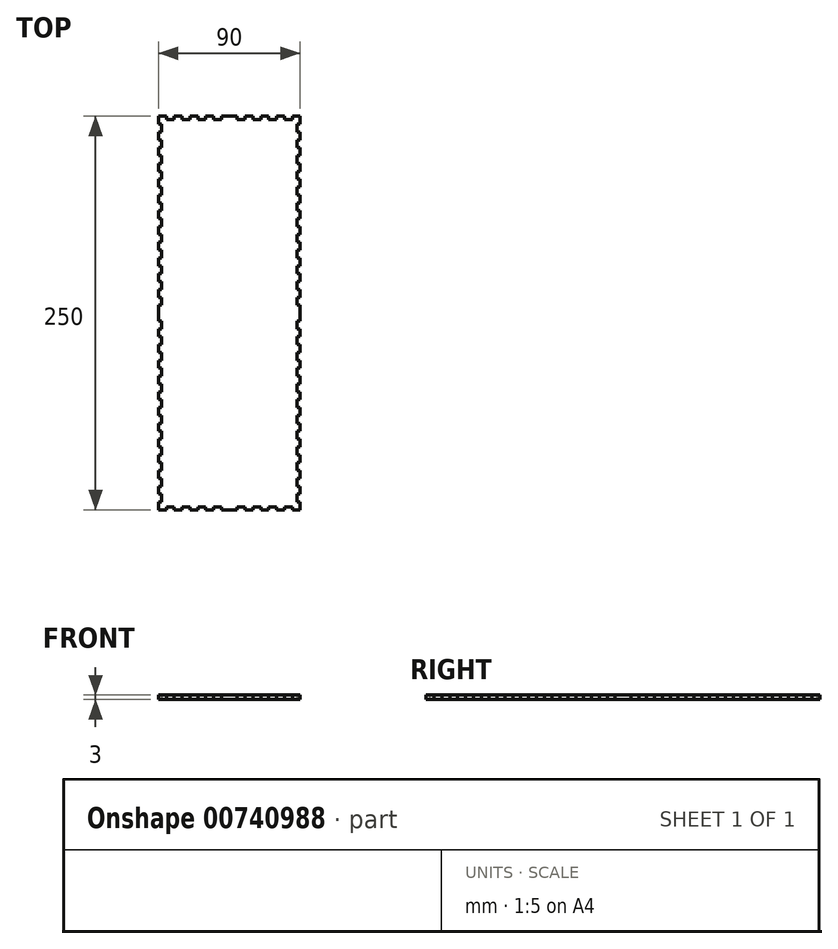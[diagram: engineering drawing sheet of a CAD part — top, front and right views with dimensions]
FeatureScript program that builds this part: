
annotation { "Feature Type Name" : "Feature", "Feature Type Description" : "" }
export const myFeature = defineFeature(function(context is Context, id is Id, definition is map)
    precondition{}
    {
        {
            var Q0;
            Q0=qCreatedBy(makeId("Top.planeOp"),FACE);
            var sketch = newSketch(context, id + "F0", { "sketchPlane" : qUnion([Q0])});
            skLineSegment(sketch, "E0.bottom", {"start": v(-45, 125) * mm, "end": v(-40, 125) * mm});
            skLineSegment(sketch, "E0.top", {"start": v(-45, -125) * mm, "end": v(-40, -125) * mm});
            skLineSegment(sketch, "E0.left", {"start": v(-45, 125) * mm, "end": v(-45, 120) * mm});
            skLineSegment(sketch, "E0.right", {"start": v(45, 125) * mm, "end": v(45, 120) * mm});
            skPoint(sketch, "E1", {"position": v(0, 0) * mm});
            skLineSegment(sketch, "E2", {"start": v(-45, 125) * mm, "end": v(45, -125) * mm, "construction": true});
            skLineSegment(sketch, "E3", {"start": v(45, 125) * mm, "end": v(-45, -125) * mm, "construction": true});
            skLineSegment(sketch, "E4.top", {"start": v(-40, 123) * mm, "end": v(-35, 123) * mm});
            skLineSegment(sketch, "E4.left", {"start": v(-40, 125) * mm, "end": v(-40, 123) * mm});
            skLineSegment(sketch, "E4.right", {"start": v(-35, 125) * mm, "end": v(-35, 123) * mm});
            skLineSegment(sketch, "E5.top", {"start": v(-30, 123) * mm, "end": v(-25, 123) * mm});
            skLineSegment(sketch, "E5.left", {"start": v(-30, 125) * mm, "end": v(-30, 123) * mm});
            skLineSegment(sketch, "E5.right", {"start": v(-25, 125) * mm, "end": v(-25, 123) * mm});
            skLineSegment(sketch, "E6", {"start": v(-45, 0) * mm, "end": v(45, 0) * mm, "construction": true});
            skLineSegment(sketch, "E7.top", {"start": v(-20, 123) * mm, "end": v(-15, 123) * mm});
            skLineSegment(sketch, "E7.left", {"start": v(-20, 125) * mm, "end": v(-20, 123) * mm});
            skLineSegment(sketch, "E7.right", {"start": v(-15, 125) * mm, "end": v(-15, 123) * mm});
            skLineSegment(sketch, "E8.top", {"start": v(-10, 123) * mm, "end": v(-5, 123) * mm});
            skLineSegment(sketch, "E8.left", {"start": v(-10, 125) * mm, "end": v(-10, 123) * mm});
            skLineSegment(sketch, "E8.right", {"start": v(-5, 125) * mm, "end": v(-5, 123) * mm});
            skLineSegment(sketch, "E9.top", {"start": v(5, 123) * mm, "end": v(10, 123) * mm});
            skLineSegment(sketch, "E9.left", {"start": v(5, 125) * mm, "end": v(5, 123) * mm});
            skLineSegment(sketch, "E9.right", {"start": v(10, 125) * mm, "end": v(10, 123) * mm});
            skLineSegment(sketch, "E10.top", {"start": v(15, 123) * mm, "end": v(20, 123) * mm});
            skLineSegment(sketch, "E10.left", {"start": v(15, 125) * mm, "end": v(15, 123) * mm});
            skLineSegment(sketch, "E10.right", {"start": v(20, 125) * mm, "end": v(20, 123) * mm});
            skLineSegment(sketch, "E11.top", {"start": v(25, 123) * mm, "end": v(30, 123) * mm});
            skLineSegment(sketch, "E11.left", {"start": v(25, 125) * mm, "end": v(25, 123) * mm});
            skLineSegment(sketch, "E11.right", {"start": v(30, 125) * mm, "end": v(30, 123) * mm});
            skLineSegment(sketch, "E12.top", {"start": v(35, 123) * mm, "end": v(40, 123) * mm});
            skLineSegment(sketch, "E12.left", {"start": v(35, 125) * mm, "end": v(35, 123) * mm});
            skLineSegment(sketch, "E12.right", {"start": v(40, 125) * mm, "end": v(40, 123) * mm});
            skLineSegment(sketch, "E13.bottom", {"start": v(-40, -123) * mm, "end": v(-35, -123) * mm});
            skLineSegment(sketch, "E13.left", {"start": v(-40, -123) * mm, "end": v(-40, -125) * mm});
            skLineSegment(sketch, "E13.right", {"start": v(-35, -123) * mm, "end": v(-35, -125) * mm});
            skLineSegment(sketch, "E14.bottom", {"start": v(-30, -123) * mm, "end": v(-25, -123) * mm});
            skLineSegment(sketch, "E14.left", {"start": v(-30, -123) * mm, "end": v(-30, -125) * mm});
            skLineSegment(sketch, "E14.right", {"start": v(-25, -123) * mm, "end": v(-25, -125) * mm});
            skLineSegment(sketch, "E15.bottom", {"start": v(-20, -123) * mm, "end": v(-15, -123) * mm});
            skLineSegment(sketch, "E15.left", {"start": v(-20, -123) * mm, "end": v(-20, -125) * mm});
            skLineSegment(sketch, "E15.right", {"start": v(-15, -123) * mm, "end": v(-15, -125) * mm});
            skLineSegment(sketch, "E16.bottom", {"start": v(-10, -123) * mm, "end": v(-5, -123) * mm});
            skLineSegment(sketch, "E16.left", {"start": v(-10, -123) * mm, "end": v(-10, -125) * mm});
            skLineSegment(sketch, "E16.right", {"start": v(-5, -123) * mm, "end": v(-5, -125) * mm});
            skLineSegment(sketch, "E17.bottom", {"start": v(5, -123) * mm, "end": v(10, -123) * mm});
            skLineSegment(sketch, "E17.left", {"start": v(5, -123) * mm, "end": v(5, -125) * mm});
            skLineSegment(sketch, "E17.right", {"start": v(10, -123) * mm, "end": v(10, -125) * mm});
            skLineSegment(sketch, "E18.bottom", {"start": v(15, -123) * mm, "end": v(20, -123) * mm});
            skLineSegment(sketch, "E18.left", {"start": v(15, -123) * mm, "end": v(15, -125) * mm});
            skLineSegment(sketch, "E18.right", {"start": v(20, -123) * mm, "end": v(20, -125) * mm});
            skLineSegment(sketch, "E19.bottom", {"start": v(25, -123) * mm, "end": v(30, -123) * mm});
            skLineSegment(sketch, "E19.left", {"start": v(25, -123) * mm, "end": v(25, -125) * mm});
            skLineSegment(sketch, "E19.right", {"start": v(30, -123) * mm, "end": v(30, -125) * mm});
            skLineSegment(sketch, "E20.bottom", {"start": v(35, -123) * mm, "end": v(40, -123) * mm});
            skLineSegment(sketch, "E20.left", {"start": v(35, -123) * mm, "end": v(35, -125) * mm});
            skLineSegment(sketch, "E20.right", {"start": v(40, -123) * mm, "end": v(40, -125) * mm});
            skLineSegment(sketch, "E21.bottom", {"start": v(43, 45) * mm, "end": v(43, 50) * mm});
            skLineSegment(sketch, "E21.left", {"start": v(43, 45) * mm, "end": v(45, 45) * mm});
            skLineSegment(sketch, "E21.right", {"start": v(43, 50) * mm, "end": v(45, 50) * mm});
            skLineSegment(sketch, "E22.bottom", {"start": v(43, 55) * mm, "end": v(43, 60) * mm});
            skLineSegment(sketch, "E22.left", {"start": v(43, 55) * mm, "end": v(45, 55) * mm});
            skLineSegment(sketch, "E22.right", {"start": v(43, 60) * mm, "end": v(45, 60) * mm});
            skLineSegment(sketch, "E23.bottom", {"start": v(43, 65) * mm, "end": v(43, 70) * mm});
            skLineSegment(sketch, "E23.left", {"start": v(43, 65) * mm, "end": v(45, 65) * mm});
            skLineSegment(sketch, "E23.right", {"start": v(43, 70) * mm, "end": v(45, 70) * mm});
            skLineSegment(sketch, "E24.bottom", {"start": v(43, 75) * mm, "end": v(43, 80) * mm});
            skLineSegment(sketch, "E24.left", {"start": v(43, 75) * mm, "end": v(45, 75) * mm});
            skLineSegment(sketch, "E24.right", {"start": v(43, 80) * mm, "end": v(45, 80) * mm});
            skLineSegment(sketch, "E25.bottom", {"start": v(43, 85) * mm, "end": v(43, 90) * mm});
            skLineSegment(sketch, "E25.left", {"start": v(43, 85) * mm, "end": v(45, 85) * mm});
            skLineSegment(sketch, "E25.right", {"start": v(43, 90) * mm, "end": v(45, 90) * mm});
            skLineSegment(sketch, "E26.bottom", {"start": v(43, 95) * mm, "end": v(43, 100) * mm});
            skLineSegment(sketch, "E26.left", {"start": v(43, 95) * mm, "end": v(45, 95) * mm});
            skLineSegment(sketch, "E26.right", {"start": v(43, 100) * mm, "end": v(45, 100) * mm});
            skLineSegment(sketch, "E27.bottom", {"start": v(43, 105) * mm, "end": v(43, 110) * mm});
            skLineSegment(sketch, "E27.left", {"start": v(43, 105) * mm, "end": v(45, 105) * mm});
            skLineSegment(sketch, "E27.right", {"start": v(43, 110) * mm, "end": v(45, 110) * mm});
            skLineSegment(sketch, "E28.bottom", {"start": v(43, 115) * mm, "end": v(43, 120) * mm});
            skLineSegment(sketch, "E28.left", {"start": v(43, 115) * mm, "end": v(45, 115) * mm});
            skLineSegment(sketch, "E28.right", {"start": v(43, 120) * mm, "end": v(45, 120) * mm});
            skLineSegment(sketch, "E29.bottom", {"start": v(43, 15) * mm, "end": v(43, 20) * mm});
            skLineSegment(sketch, "E29.left", {"start": v(43, 15) * mm, "end": v(45, 15) * mm});
            skLineSegment(sketch, "E29.right", {"start": v(43, 20) * mm, "end": v(45, 20) * mm});
            skLineSegment(sketch, "E30.bottom", {"start": v(43, 25) * mm, "end": v(43, 30) * mm});
            skLineSegment(sketch, "E30.left", {"start": v(43, 25) * mm, "end": v(45, 25) * mm});
            skLineSegment(sketch, "E30.right", {"start": v(43, 30) * mm, "end": v(45, 30) * mm});
            skLineSegment(sketch, "E31.bottom", {"start": v(43, 35) * mm, "end": v(43, 40) * mm});
            skLineSegment(sketch, "E31.left", {"start": v(43, 35) * mm, "end": v(45, 35) * mm});
            skLineSegment(sketch, "E31.right", {"start": v(43, 40) * mm, "end": v(45, 40) * mm});
            skLineSegment(sketch, "E32.bottom", {"start": v(43, -90) * mm, "end": v(43, -85) * mm});
            skLineSegment(sketch, "E32.left", {"start": v(43, -90) * mm, "end": v(45, -90) * mm});
            skLineSegment(sketch, "E32.right", {"start": v(43, -85) * mm, "end": v(45, -85) * mm});
            skLineSegment(sketch, "E33.bottom", {"start": v(43, -80) * mm, "end": v(43, -75) * mm});
            skLineSegment(sketch, "E33.left", {"start": v(43, -80) * mm, "end": v(45, -80) * mm});
            skLineSegment(sketch, "E33.right", {"start": v(43, -75) * mm, "end": v(45, -75) * mm});
            skLineSegment(sketch, "E34.bottom", {"start": v(43, -70) * mm, "end": v(43, -65) * mm});
            skLineSegment(sketch, "E34.left", {"start": v(43, -70) * mm, "end": v(45, -70) * mm});
            skLineSegment(sketch, "E34.right", {"start": v(43, -65) * mm, "end": v(45, -65) * mm});
            skLineSegment(sketch, "E35.bottom", {"start": v(43, -60) * mm, "end": v(43, -55) * mm});
            skLineSegment(sketch, "E35.left", {"start": v(43, -60) * mm, "end": v(45, -60) * mm});
            skLineSegment(sketch, "E35.right", {"start": v(43, -55) * mm, "end": v(45, -55) * mm});
            skLineSegment(sketch, "E36.bottom", {"start": v(43, -50) * mm, "end": v(43, -45) * mm});
            skLineSegment(sketch, "E36.left", {"start": v(43, -50) * mm, "end": v(45, -50) * mm});
            skLineSegment(sketch, "E36.right", {"start": v(43, -45) * mm, "end": v(45, -45) * mm});
            skLineSegment(sketch, "E37.bottom", {"start": v(43, -40) * mm, "end": v(43, -35) * mm});
            skLineSegment(sketch, "E37.left", {"start": v(43, -40) * mm, "end": v(45, -40) * mm});
            skLineSegment(sketch, "E37.right", {"start": v(43, -35) * mm, "end": v(45, -35) * mm});
            skLineSegment(sketch, "E38.bottom", {"start": v(43, -30) * mm, "end": v(43, -25) * mm});
            skLineSegment(sketch, "E38.left", {"start": v(43, -30) * mm, "end": v(45, -30) * mm});
            skLineSegment(sketch, "E38.right", {"start": v(43, -25) * mm, "end": v(45, -25) * mm});
            skLineSegment(sketch, "E39.bottom", {"start": v(43, -20) * mm, "end": v(43, -15) * mm});
            skLineSegment(sketch, "E39.left", {"start": v(43, -20) * mm, "end": v(45, -20) * mm});
            skLineSegment(sketch, "E39.right", {"start": v(43, -15) * mm, "end": v(45, -15) * mm});
            skLineSegment(sketch, "E40.bottom", {"start": v(43, -120) * mm, "end": v(43, -115) * mm});
            skLineSegment(sketch, "E40.left", {"start": v(43, -120) * mm, "end": v(45, -120) * mm});
            skLineSegment(sketch, "E40.right", {"start": v(43, -115) * mm, "end": v(45, -115) * mm});
            skLineSegment(sketch, "E41.bottom", {"start": v(43, -110) * mm, "end": v(43, -105) * mm});
            skLineSegment(sketch, "E41.left", {"start": v(43, -110) * mm, "end": v(45, -110) * mm});
            skLineSegment(sketch, "E41.right", {"start": v(43, -105) * mm, "end": v(45, -105) * mm});
            skLineSegment(sketch, "E42.bottom", {"start": v(43, -100) * mm, "end": v(43, -95) * mm});
            skLineSegment(sketch, "E42.left", {"start": v(43, -100) * mm, "end": v(45, -100) * mm});
            skLineSegment(sketch, "E42.right", {"start": v(43, -95) * mm, "end": v(45, -95) * mm});
            skLineSegment(sketch, "E43.top", {"start": v(-43, 45) * mm, "end": v(-43, 50) * mm});
            skLineSegment(sketch, "E43.left", {"start": v(-45, 45) * mm, "end": v(-43, 45) * mm});
            skLineSegment(sketch, "E43.right", {"start": v(-45, 50) * mm, "end": v(-43, 50) * mm});
            skLineSegment(sketch, "E44.top", {"start": v(-43, 55) * mm, "end": v(-43, 60) * mm});
            skLineSegment(sketch, "E44.left", {"start": v(-45, 55) * mm, "end": v(-43, 55) * mm});
            skLineSegment(sketch, "E44.right", {"start": v(-45, 60) * mm, "end": v(-43, 60) * mm});
            skLineSegment(sketch, "E45.top", {"start": v(-43, 65) * mm, "end": v(-43, 70) * mm});
            skLineSegment(sketch, "E45.left", {"start": v(-45, 65) * mm, "end": v(-43, 65) * mm});
            skLineSegment(sketch, "E45.right", {"start": v(-45, 70) * mm, "end": v(-43, 70) * mm});
            skLineSegment(sketch, "E46.top", {"start": v(-43, 75) * mm, "end": v(-43, 80) * mm});
            skLineSegment(sketch, "E46.left", {"start": v(-45, 75) * mm, "end": v(-43, 75) * mm});
            skLineSegment(sketch, "E46.right", {"start": v(-45, 80) * mm, "end": v(-43, 80) * mm});
            skLineSegment(sketch, "E47.top", {"start": v(-43, 85) * mm, "end": v(-43, 90) * mm});
            skLineSegment(sketch, "E47.left", {"start": v(-45, 85) * mm, "end": v(-43, 85) * mm});
            skLineSegment(sketch, "E47.right", {"start": v(-45, 90) * mm, "end": v(-43, 90) * mm});
            skLineSegment(sketch, "E48.top", {"start": v(-43, 95) * mm, "end": v(-43, 100) * mm});
            skLineSegment(sketch, "E48.left", {"start": v(-45, 95) * mm, "end": v(-43, 95) * mm});
            skLineSegment(sketch, "E48.right", {"start": v(-45, 100) * mm, "end": v(-43, 100) * mm});
            skLineSegment(sketch, "E49.top", {"start": v(-43, 105) * mm, "end": v(-43, 110) * mm});
            skLineSegment(sketch, "E49.left", {"start": v(-45, 105) * mm, "end": v(-43, 105) * mm});
            skLineSegment(sketch, "E49.right", {"start": v(-45, 110) * mm, "end": v(-43, 110) * mm});
            skLineSegment(sketch, "E50.top", {"start": v(-43, 115) * mm, "end": v(-43, 120) * mm});
            skLineSegment(sketch, "E50.left", {"start": v(-45, 115) * mm, "end": v(-43, 115) * mm});
            skLineSegment(sketch, "E50.right", {"start": v(-45, 120) * mm, "end": v(-43, 120) * mm});
            skLineSegment(sketch, "E51.top", {"start": v(-43, 15) * mm, "end": v(-43, 20) * mm});
            skLineSegment(sketch, "E51.left", {"start": v(-45, 15) * mm, "end": v(-43, 15) * mm});
            skLineSegment(sketch, "E51.right", {"start": v(-45, 20) * mm, "end": v(-43, 20) * mm});
            skLineSegment(sketch, "E52.top", {"start": v(-43, 25) * mm, "end": v(-43, 30) * mm});
            skLineSegment(sketch, "E52.left", {"start": v(-45, 25) * mm, "end": v(-43, 25) * mm});
            skLineSegment(sketch, "E52.right", {"start": v(-45, 30) * mm, "end": v(-43, 30) * mm});
            skLineSegment(sketch, "E53.top", {"start": v(-43, 35) * mm, "end": v(-43, 40) * mm});
            skLineSegment(sketch, "E53.left", {"start": v(-45, 35) * mm, "end": v(-43, 35) * mm});
            skLineSegment(sketch, "E53.right", {"start": v(-45, 40) * mm, "end": v(-43, 40) * mm});
            skLineSegment(sketch, "E54.top", {"start": v(-43, -90) * mm, "end": v(-43, -85) * mm});
            skLineSegment(sketch, "E54.left", {"start": v(-45, -90) * mm, "end": v(-43, -90) * mm});
            skLineSegment(sketch, "E54.right", {"start": v(-45, -85) * mm, "end": v(-43, -85) * mm});
            skLineSegment(sketch, "E55.top", {"start": v(-43, -80) * mm, "end": v(-43, -75) * mm});
            skLineSegment(sketch, "E55.left", {"start": v(-45, -80) * mm, "end": v(-43, -80) * mm});
            skLineSegment(sketch, "E55.right", {"start": v(-45, -75) * mm, "end": v(-43, -75) * mm});
            skLineSegment(sketch, "E56.top", {"start": v(-43, -70) * mm, "end": v(-43, -65) * mm});
            skLineSegment(sketch, "E56.left", {"start": v(-45, -70) * mm, "end": v(-43, -70) * mm});
            skLineSegment(sketch, "E56.right", {"start": v(-45, -65) * mm, "end": v(-43, -65) * mm});
            skLineSegment(sketch, "E57.top", {"start": v(-43, -60) * mm, "end": v(-43, -55) * mm});
            skLineSegment(sketch, "E57.left", {"start": v(-45, -60) * mm, "end": v(-43, -60) * mm});
            skLineSegment(sketch, "E57.right", {"start": v(-45, -55) * mm, "end": v(-43, -55) * mm});
            skLineSegment(sketch, "E58.top", {"start": v(-43, -50) * mm, "end": v(-43, -45) * mm});
            skLineSegment(sketch, "E58.left", {"start": v(-45, -50) * mm, "end": v(-43, -50) * mm});
            skLineSegment(sketch, "E58.right", {"start": v(-45, -45) * mm, "end": v(-43, -45) * mm});
            skLineSegment(sketch, "E59.top", {"start": v(-43, -40) * mm, "end": v(-43, -35) * mm});
            skLineSegment(sketch, "E59.left", {"start": v(-45, -40) * mm, "end": v(-43, -40) * mm});
            skLineSegment(sketch, "E59.right", {"start": v(-45, -35) * mm, "end": v(-43, -35) * mm});
            skLineSegment(sketch, "E60.top", {"start": v(-43, -30) * mm, "end": v(-43, -25) * mm});
            skLineSegment(sketch, "E60.left", {"start": v(-45, -30) * mm, "end": v(-43, -30) * mm});
            skLineSegment(sketch, "E60.right", {"start": v(-45, -25) * mm, "end": v(-43, -25) * mm});
            skLineSegment(sketch, "E61.top", {"start": v(-43, -20) * mm, "end": v(-43, -15) * mm});
            skLineSegment(sketch, "E61.left", {"start": v(-45, -20) * mm, "end": v(-43, -20) * mm});
            skLineSegment(sketch, "E61.right", {"start": v(-45, -15) * mm, "end": v(-43, -15) * mm});
            skLineSegment(sketch, "E62.top", {"start": v(-43, -120) * mm, "end": v(-43, -115) * mm});
            skLineSegment(sketch, "E62.left", {"start": v(-45, -120) * mm, "end": v(-43, -120) * mm});
            skLineSegment(sketch, "E62.right", {"start": v(-45, -115) * mm, "end": v(-43, -115) * mm});
            skLineSegment(sketch, "E63.top", {"start": v(-43, -110) * mm, "end": v(-43, -105) * mm});
            skLineSegment(sketch, "E63.left", {"start": v(-45, -110) * mm, "end": v(-43, -110) * mm});
            skLineSegment(sketch, "E63.right", {"start": v(-45, -105) * mm, "end": v(-43, -105) * mm});
            skLineSegment(sketch, "E64.top", {"start": v(-43, -100) * mm, "end": v(-43, -95) * mm});
            skLineSegment(sketch, "E64.left", {"start": v(-45, -100) * mm, "end": v(-43, -100) * mm});
            skLineSegment(sketch, "E64.right", {"start": v(-45, -95) * mm, "end": v(-43, -95) * mm});
            skLineSegment(sketch, "E65.top", {"start": v(-43, 5) * mm, "end": v(-43, 10) * mm});
            skLineSegment(sketch, "E65.left", {"start": v(-45, 5) * mm, "end": v(-43, 5) * mm});
            skLineSegment(sketch, "E65.right", {"start": v(-45, 10) * mm, "end": v(-43, 10) * mm});
            skLineSegment(sketch, "E66.top", {"start": v(-43, -10) * mm, "end": v(-43, -5) * mm});
            skLineSegment(sketch, "E66.left", {"start": v(-45, -10) * mm, "end": v(-43, -10) * mm});
            skLineSegment(sketch, "E66.right", {"start": v(-45, -5) * mm, "end": v(-43, -5) * mm});
            skLineSegment(sketch, "E67.bottom", {"start": v(43, -10) * mm, "end": v(43, -5) * mm});
            skLineSegment(sketch, "E67.left", {"start": v(43, -10) * mm, "end": v(45, -10) * mm});
            skLineSegment(sketch, "E67.right", {"start": v(43, -5) * mm, "end": v(45, -5) * mm});
            skLineSegment(sketch, "E68.bottom", {"start": v(43, 5) * mm, "end": v(43, 10) * mm});
            skLineSegment(sketch, "E68.left", {"start": v(43, 5) * mm, "end": v(45, 5) * mm});
            skLineSegment(sketch, "E68.right", {"start": v(43, 10) * mm, "end": v(45, 10) * mm});
            skLineSegment(sketch, "E69.trimOffspring", {"start": v(-35, 125) * mm, "end": v(-30, 125) * mm});
            skLineSegment(sketch, "E70.trimOffspring", {"start": v(-25, 125) * mm, "end": v(-20, 125) * mm});
            skLineSegment(sketch, "E71.trimOffspring", {"start": v(-15, 125) * mm, "end": v(-10, 125) * mm});
            skLineSegment(sketch, "E72.trimOffspring", {"start": v(-5, 125) * mm, "end": v(5, 125) * mm});
            skLineSegment(sketch, "E73.trimOffspring", {"start": v(10, 125) * mm, "end": v(15, 125) * mm});
            skLineSegment(sketch, "E74.trimOffspring", {"start": v(20, 125) * mm, "end": v(25, 125) * mm});
            skLineSegment(sketch, "E75.trimOffspring", {"start": v(30, 125) * mm, "end": v(35, 125) * mm});
            skLineSegment(sketch, "E76.trimOffspring", {"start": v(40, 125) * mm, "end": v(45, 125) * mm});
            skLineSegment(sketch, "E77.trimOffspring", {"start": v(45, 115) * mm, "end": v(45, 110) * mm});
            skLineSegment(sketch, "E78.trimOffspring", {"start": v(45, 105) * mm, "end": v(45, 100) * mm});
            skLineSegment(sketch, "E79.trimOffspring", {"start": v(45, 95) * mm, "end": v(45, 90) * mm});
            skLineSegment(sketch, "E80.trimOffspring", {"start": v(45, 85) * mm, "end": v(45, 80) * mm});
            skLineSegment(sketch, "E81.trimOffspring", {"start": v(45, 75) * mm, "end": v(45, 70) * mm});
            skLineSegment(sketch, "E82.trimOffspring", {"start": v(45, 65) * mm, "end": v(45, 60) * mm});
            skLineSegment(sketch, "E83.trimOffspring", {"start": v(45, 55) * mm, "end": v(45, 50) * mm});
            skLineSegment(sketch, "E84.trimOffspring", {"start": v(45, 45) * mm, "end": v(45, 40) * mm});
            skLineSegment(sketch, "E85.trimOffspring", {"start": v(45, 35) * mm, "end": v(45, 30) * mm});
            skLineSegment(sketch, "E86.trimOffspring", {"start": v(45, 25) * mm, "end": v(45, 20) * mm});
            skLineSegment(sketch, "E87.trimOffspring", {"start": v(45, 15) * mm, "end": v(45, 10) * mm});
            skLineSegment(sketch, "E88.trimOffspring", {"start": v(45, 5) * mm, "end": v(45, -5) * mm});
            skLineSegment(sketch, "E89.trimOffspring", {"start": v(45, -10) * mm, "end": v(45, -15) * mm});
            skLineSegment(sketch, "E90.trimOffspring", {"start": v(45, -20) * mm, "end": v(45, -25) * mm});
            skLineSegment(sketch, "E91.trimOffspring", {"start": v(45, -30) * mm, "end": v(45, -35) * mm});
            skLineSegment(sketch, "E92.trimOffspring", {"start": v(45, -40) * mm, "end": v(45, -45) * mm});
            skLineSegment(sketch, "E93.trimOffspring", {"start": v(45, -50) * mm, "end": v(45, -55) * mm});
            skLineSegment(sketch, "E94.trimOffspring", {"start": v(45, -60) * mm, "end": v(45, -65) * mm});
            skLineSegment(sketch, "E95.trimOffspring", {"start": v(45, -70) * mm, "end": v(45, -75) * mm});
            skLineSegment(sketch, "E96.trimOffspring", {"start": v(45, -80) * mm, "end": v(45, -85) * mm});
            skLineSegment(sketch, "E97.trimOffspring", {"start": v(45, -90) * mm, "end": v(45, -95) * mm});
            skLineSegment(sketch, "E98.trimOffspring", {"start": v(45, -100) * mm, "end": v(45, -105) * mm});
            skLineSegment(sketch, "E99.trimOffspring", {"start": v(45, -110) * mm, "end": v(45, -115) * mm});
            skLineSegment(sketch, "E100.trimOffspring", {"start": v(45, -120) * mm, "end": v(45, -125) * mm});
            skLineSegment(sketch, "E101.trimOffspring", {"start": v(40, -125) * mm, "end": v(45, -125) * mm});
            skLineSegment(sketch, "E102.trimOffspring", {"start": v(30, -125) * mm, "end": v(35, -125) * mm});
            skLineSegment(sketch, "E103.trimOffspring", {"start": v(20, -125) * mm, "end": v(25, -125) * mm});
            skLineSegment(sketch, "E104.trimOffspring", {"start": v(10, -125) * mm, "end": v(15, -125) * mm});
            skLineSegment(sketch, "E105.trimOffspring", {"start": v(-5, -125) * mm, "end": v(5, -125) * mm});
            skLineSegment(sketch, "E106.trimOffspring", {"start": v(-15, -125) * mm, "end": v(-10, -125) * mm});
            skLineSegment(sketch, "E107.trimOffspring", {"start": v(-25, -125) * mm, "end": v(-20, -125) * mm});
            skLineSegment(sketch, "E108.trimOffspring", {"start": v(-35, -125) * mm, "end": v(-30, -125) * mm});
            skLineSegment(sketch, "E109.trimOffspring", {"start": v(-45, -120) * mm, "end": v(-45, -125) * mm});
            skLineSegment(sketch, "E110.trimOffspring", {"start": v(-45, -110) * mm, "end": v(-45, -115) * mm});
            skLineSegment(sketch, "E111.trimOffspring", {"start": v(-45, -100) * mm, "end": v(-45, -105) * mm});
            skLineSegment(sketch, "E112.trimOffspring", {"start": v(-45, -90) * mm, "end": v(-45, -95) * mm});
            skLineSegment(sketch, "E113.trimOffspring", {"start": v(-45, -80) * mm, "end": v(-45, -85) * mm});
            skLineSegment(sketch, "E114.trimOffspring", {"start": v(-45, -70) * mm, "end": v(-45, -75) * mm});
            skLineSegment(sketch, "E115.trimOffspring", {"start": v(-45, -60) * mm, "end": v(-45, -65) * mm});
            skLineSegment(sketch, "E116.trimOffspring", {"start": v(-45, -50) * mm, "end": v(-45, -55) * mm});
            skLineSegment(sketch, "E117.trimOffspring", {"start": v(-45, -40) * mm, "end": v(-45, -45) * mm});
            skLineSegment(sketch, "E118.trimOffspring", {"start": v(-45, -30) * mm, "end": v(-45, -35) * mm});
            skLineSegment(sketch, "E119.trimOffspring", {"start": v(-45, -20) * mm, "end": v(-45, -25) * mm});
            skLineSegment(sketch, "E120.trimOffspring", {"start": v(-45, -10) * mm, "end": v(-45, -15) * mm});
            skLineSegment(sketch, "E121.trimOffspring", {"start": v(-45, 5) * mm, "end": v(-45, -5) * mm});
            skLineSegment(sketch, "E122.trimOffspring", {"start": v(-45, 15) * mm, "end": v(-45, 10) * mm});
            skLineSegment(sketch, "E123.trimOffspring", {"start": v(-45, 25) * mm, "end": v(-45, 20) * mm});
            skLineSegment(sketch, "E124.trimOffspring", {"start": v(-45, 35) * mm, "end": v(-45, 30) * mm});
            skLineSegment(sketch, "E125.trimOffspring", {"start": v(-45, 45) * mm, "end": v(-45, 40) * mm});
            skLineSegment(sketch, "E126.trimOffspring", {"start": v(-45, 55) * mm, "end": v(-45, 50) * mm});
            skLineSegment(sketch, "E127.trimOffspring", {"start": v(-45, 65) * mm, "end": v(-45, 60) * mm});
            skLineSegment(sketch, "E128.trimOffspring", {"start": v(-45, 75) * mm, "end": v(-45, 70) * mm});
            skLineSegment(sketch, "E129.trimOffspring", {"start": v(-45, 85) * mm, "end": v(-45, 80) * mm});
            skLineSegment(sketch, "E130.trimOffspring", {"start": v(-45, 95) * mm, "end": v(-45, 90) * mm});
            skLineSegment(sketch, "E131.trimOffspring", {"start": v(-45, 105) * mm, "end": v(-45, 100) * mm});
            skLineSegment(sketch, "E132.trimOffspring", {"start": v(-45, 115) * mm, "end": v(-45, 110) * mm});
            skSolve(sketch);
        }
        {
            var Q0;
            Q0 = qSketchRegion(id + "F0", true);
            extrude(context, id + "F1", {"entities" : qUnion([Q0]), "depth" : 3 * mm, "offsetDistance" : 25 * mm});
        }
    });
